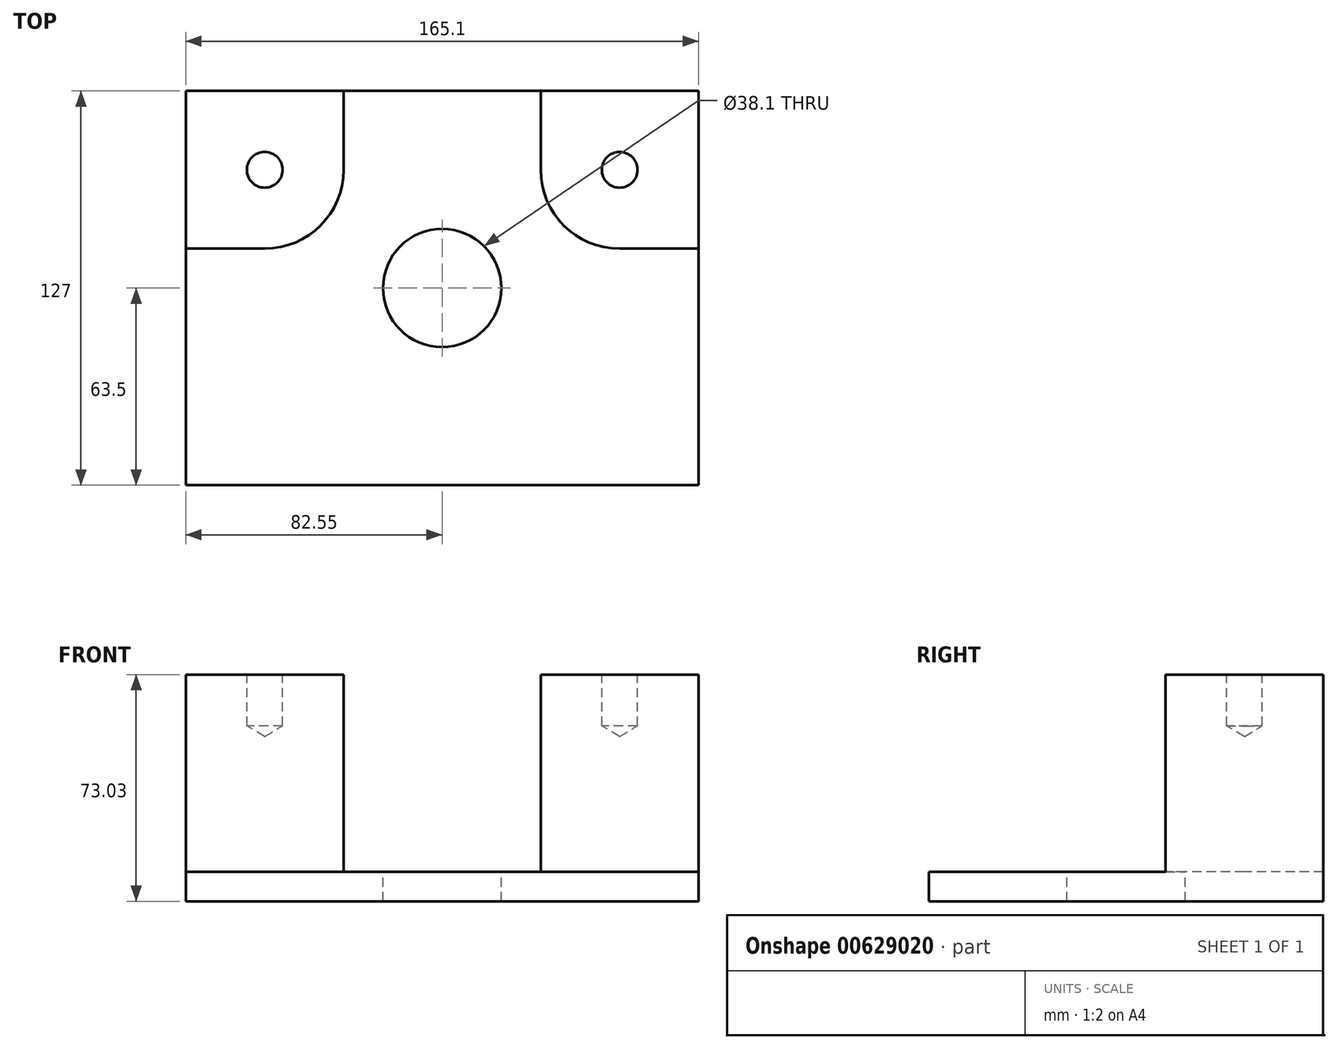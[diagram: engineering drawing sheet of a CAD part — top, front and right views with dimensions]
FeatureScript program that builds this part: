
annotation { "Feature Type Name" : "Feature", "Feature Type Description" : "" }
export const myFeature = defineFeature(function(context is Context, id is Id, definition is map)
    precondition{}
    {
        {
            var Q0;
            Q0=qCreatedBy(makeId("Top.planeOp"),FACE);
            var sketch = newSketch(context, id + "F0", { "sketchPlane" : qUnion([Q0])});
            skLineSegment(sketch, "E0.bottom", {"start": v(-82.55, 63.5) * mm, "end": v(82.55, 63.5) * mm});
            skLineSegment(sketch, "E0.top", {"start": v(-82.55, -63.5) * mm, "end": v(82.55, -63.5) * mm});
            skLineSegment(sketch, "E0.left", {"start": v(-82.55, 63.5) * mm, "end": v(-82.55, -63.5) * mm});
            skLineSegment(sketch, "E0.right", {"start": v(82.55, 63.5) * mm, "end": v(82.55, -63.5) * mm});
            skPoint(sketch, "E0.middle", {"position": v(0, 0) * mm});
            skCircle(sketch, "E1", {"center": v(0, 0) * mm, "radius": 19.05 * mm});
            skSolve(sketch);
        }
        {
            var Q0;
            Q0=makeQuery(id+"F0.imprint","IMPRINT",FACE,{"disambiguationData":[TD([[makeQuery(id+"F0.imprint","IMPRINT",EDGE,{"derivedFrom":sQuery(id+"F0.wireOp",EDGE,"E0.bottom")}),-1.0]])]});
            extrude(context, id + "F1", {"entities" : qUnion([Q0]), "oppositeDirection" : true, "depth" : 9.52 * mm, "offsetDistance" : 25.4 * mm});
        }
        {
            var Q0;
            Q0=makeQuery(id+"F1.opExtrude","CAP_FACE",FACE,{"disambiguationData":[OSD([sQuery(id+"F0.wireOp",EDGE,"E0.bottom"),sQuery(id+"F0.wireOp",EDGE,"E0.top"),sQuery(id+"F0.wireOp",EDGE,"E0.left"),sQuery(id+"F0.wireOp",EDGE,"E0.right"),sQuery(id+"F0.wireOp",EDGE,"E1")])],"isStart":true});
            var sketch = newSketch(context, id + "F2", { "sketchPlane" : qUnion([Q0])});
            skLineSegment(sketch, "E2.bottom", {"start": v(-82.55, 63.5) * mm, "end": v(-31.75, 63.5) * mm});
            skLineSegment(sketch, "E2.top", {"start": v(-82.55, 12.7) * mm, "end": v(-57.15, 12.7) * mm});
            skLineSegment(sketch, "E2.left", {"start": v(-82.55, 63.5) * mm, "end": v(-82.55, 12.7) * mm});
            skLineSegment(sketch, "E2.right", {"start": v(-31.75, 63.5) * mm, "end": v(-31.75, 38.1) * mm});
            skLineSegment(sketch, "E3.bottom", {"start": v(82.55, 63.5) * mm, "end": v(31.75, 63.5) * mm});
            skLineSegment(sketch, "E3.top", {"start": v(82.55, 12.7) * mm, "end": v(57.15, 12.7) * mm});
            skLineSegment(sketch, "E3.left", {"start": v(82.55, 63.5) * mm, "end": v(82.55, 12.7) * mm});
            skLineSegment(sketch, "E3.right", {"start": v(31.75, 63.5) * mm, "end": v(31.75, 38.1) * mm});
            skPoint(sketch, "E4.visualSharp", {"position": v(-31.75, 12.7) * mm});
            skArc(sketch, "E4.filletArc", {"start": v(-57.15, 12.7) * mm, "mid": v(-39.19, 20.14) * mm, "end": v(-31.75, 38.1) * mm});
            skPoint(sketch, "E5.visualSharp", {"position": v(31.75, 12.7) * mm});
            skArc(sketch, "E5.filletArc", {"start": v(31.75, 38.1) * mm, "mid": v(39.19, 20.14) * mm, "end": v(57.15, 12.7) * mm});
            skSolve(sketch);
        }
        {
            var Q0;
            Q0=makeQuery(id+"F2.imprint","IMPRINT",FACE,{"disambiguationData":[TD([[makeQuery(id+"F2.imprint","IMPRINT",EDGE,{"derivedFrom":sQuery(id+"F2.wireOp",EDGE,"E2.bottom")}),-1.0]])]});
            var Q1;
            Q1=makeQuery(id+"F2.imprint","IMPRINT",FACE,{"disambiguationData":[TD([[makeQuery(id+"F2.imprint","IMPRINT",EDGE,{"derivedFrom":sQuery(id+"F2.wireOp",EDGE,"E3.bottom")}),-1.0]])]});
            extrude(context, id + "F3", {"entities" : qUnion([Q0, Q1]), "operationType" : NewBodyOperationType.ADD, "depth" : 63.5 * mm, "offsetDistance" : 25.4 * mm});
        }
        {
            var Q0;
            Q0=makeQuery(id+"F3.opExtrude","CAP_FACE",FACE,{"disambiguationData":[OSD([sQuery(id+"F2.wireOp",EDGE,"E2.bottom"),sQuery(id+"F2.wireOp",EDGE,"E2.top"),sQuery(id+"F2.wireOp",EDGE,"E2.left"),sQuery(id+"F2.wireOp",EDGE,"E2.right"),sQuery(id+"F2.wireOp",EDGE,"E4.filletArc")])],"isStart":false});
            var sketch = newSketch(context, id + "F4", { "sketchPlane" : qUnion([Q0])});
            skPoint(sketch, "E6", {"position": v(-57.15, 38.1) * mm});
            skLineSegment(sketch, "E7.0.0", {"start": v(82.55, 63.5) * mm, "end": v(31.75, 63.5) * mm});
            skLineSegment(sketch, "E7.0.1", {"start": v(31.75, 63.5) * mm, "end": v(31.75, 38.1) * mm});
            skArc(sketch, "E7.0.2", {"start": v(31.75, 38.1) * mm, "mid": v(39.19, 20.14) * mm, "end": v(57.15, 12.7) * mm});
            skLineSegment(sketch, "E7.0.3", {"start": v(57.15, 12.7) * mm, "end": v(82.55, 12.7) * mm});
            skLineSegment(sketch, "E7.0.4", {"start": v(82.55, 12.7) * mm, "end": v(82.55, 63.5) * mm});
            skSolve(sketch);
        }
        {
            var Q0;
            Q0=sQuery(id+"F4.wireOp",VERTEX,"E7.0.2.center");
            var Q1;
            Q1=sQuery(id+"F4.wireOp",VERTEX,"E6");
            var Q2;
            Q2=makeQuery(id+"F1.opExtrude","SWEPT_BODY",BODY,{"disambiguationData":[OSD([sQuery(id+"F0.wireOp",EDGE,"E0.bottom"),sQuery(id+"F0.wireOp",EDGE,"E0.top"),sQuery(id+"F0.wireOp",EDGE,"E0.left"),sQuery(id+"F0.wireOp",EDGE,"E0.right"),sQuery(id+"F0.wireOp",EDGE,"E1")])]});
            hole(context, id + "F5", {"style" : HoleStyle.SIMPLE, "endStyle" : HoleEndStyle.BLIND, "standardTappedOrClearance" : lookupTablePath({ "standard" : "ANSI", "engagement" : "75%", "pitch" : "20 tpi", "size" : "1/2", "type" : "Tapped" }), "standardBlindInLast" : lookupTablePath({ "standard" : "ANSI", "engagement" : "75%", "pitch" : "20 tpi", "size" : "1/2", "type" : "Tapped" }), "holeDiameter" : 11.5 * mm, "majorDiameter" : 12.7 * mm, "showTappedDepth" : true, "holeDepth" : 16.51 * mm, "isTappedThrough" : true, "tappedDepth" : 12.7 * mm, "tapClearance" : 3, "locations" : qUnion([Q0, Q1]), "scope" : qUnion([Q2])});
        }
    });
